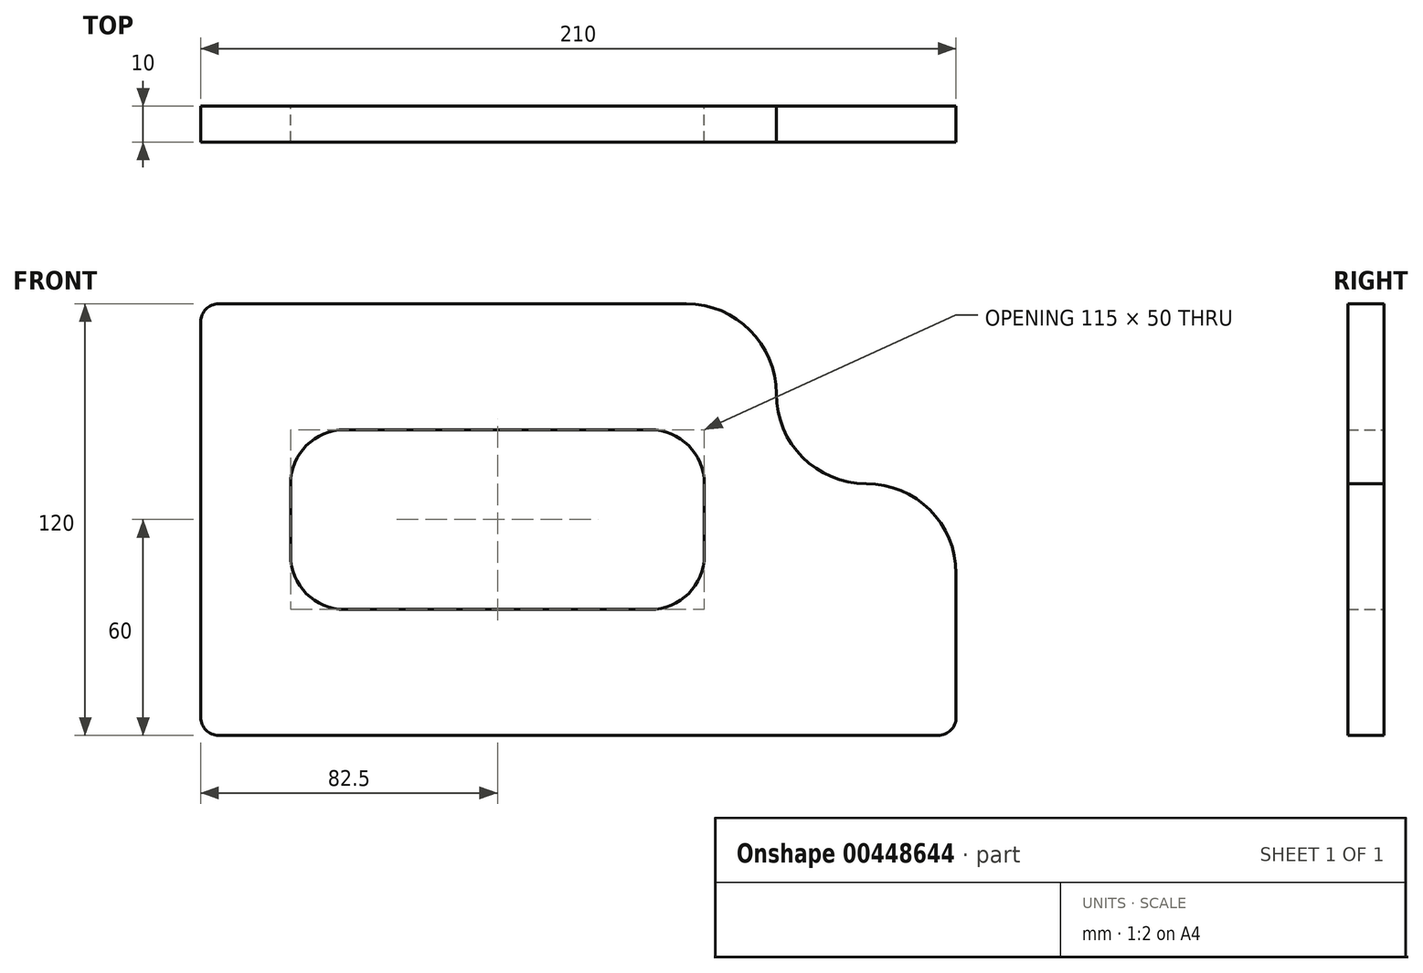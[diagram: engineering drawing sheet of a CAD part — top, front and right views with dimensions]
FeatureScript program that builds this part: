
annotation { "Feature Type Name" : "Feature", "Feature Type Description" : "" }
export const myFeature = defineFeature(function(context is Context, id is Id, definition is map)
    precondition{}
    {
        {
            var Q0;
            Q0=qCreatedBy(makeId("Front.planeOp"),FACE);
            var sketch = newSketch(context, id + "F0", { "sketchPlane" : qUnion([Q0])});
            skLineSegment(sketch, "E0.bottom", {"start": v(-105, 60) * mm, "end": v(55, 60) * mm});
            skLineSegment(sketch, "E0.top", {"start": v(-105, -60) * mm, "end": v(105, -60) * mm});
            skLineSegment(sketch, "E0.left", {"start": v(-105, 60) * mm, "end": v(-105, -60) * mm});
            skLineSegment(sketch, "E0.right", {"start": v(105, 10) * mm, "end": v(105, -60) * mm});
            skPoint(sketch, "E0.middle", {"position": v(0, 0) * mm});
            skLineSegment(sketch, "E1", {"start": v(55, 60) * mm, "end": v(55, 10) * mm});
            skLineSegment(sketch, "E2", {"start": v(55, 10) * mm, "end": v(105, 10) * mm});
            skPoint(sketch, "E3.orphan", {"position": v(105, 60) * mm});
            skLineSegment(sketch, "E4.bottom", {"start": v(-80, 25) * mm, "end": v(35, 25) * mm});
            skLineSegment(sketch, "E4.top", {"start": v(-80, -25) * mm, "end": v(35, -25) * mm});
            skLineSegment(sketch, "E4.left", {"start": v(-80, 25) * mm, "end": v(-80, -25) * mm});
            skLineSegment(sketch, "E4.right", {"start": v(35, 25) * mm, "end": v(35, -25) * mm});
            skSolve(sketch);
        }
        {
            var Q0;
            Q0=makeQuery(id+"F0.imprint","IMPRINT",FACE,{"disambiguationData":[TD([[makeQuery(id+"F0.imprint","IMPRINT",EDGE,{"derivedFrom":sQuery(id+"F0.wireOp",EDGE,"E0.bottom")}),-1.0]])]});
            extrude(context, id + "F1", {"entities" : qUnion([Q0]), "endBound" : BoundingType.SYMMETRIC, "depth" : 10 * mm});
        }
        {
            var Q0;
            Q0=makeQuery(id+"F1.opExtrude","SWEPT_EDGE",EDGE,{"disambiguationData":[OSD([sQuery(id+"F0.wireOp",EDGE,"E1"),sQuery(id+"F0.wireOp",EDGE,"E2")])]});
            var Q1;
            Q1=makeQuery(id+"F1.opExtrude","SWEPT_EDGE",EDGE,{"disambiguationData":[OSD([sQuery(id+"F0.wireOp",EDGE,"E0.right"),sQuery(id+"F0.wireOp",EDGE,"E2")])]});
            var Q2;
            Q2=makeQuery(id+"F1.opExtrude","SWEPT_EDGE",EDGE,{"disambiguationData":[OSD([sQuery(id+"F0.wireOp",EDGE,"E0.bottom"),sQuery(id+"F0.wireOp",EDGE,"E1")])]});
            fillet(context, id + "F2", {"entities" : qUnion([Q0, Q1, Q2]), "radius" : 25 * mm, "tangentPropagation" : true, "allowEdgeOverflow" : false});
        }
        {
            var Q0;
            Q0=makeQuery(id+"F1.opExtrude","SWEPT_EDGE",EDGE,{"disambiguationData":[OSD([sQuery(id+"F0.wireOp",EDGE,"E0.top"),sQuery(id+"F0.wireOp",EDGE,"E0.right")])]});
            var Q1;
            Q1=makeQuery(id+"F1.opExtrude","SWEPT_EDGE",EDGE,{"disambiguationData":[OSD([sQuery(id+"F0.wireOp",EDGE,"E0.top"),sQuery(id+"F0.wireOp",EDGE,"E0.left")])]});
            var Q2;
            Q2=makeQuery(id+"F1.opExtrude","SWEPT_EDGE",EDGE,{"disambiguationData":[OSD([sQuery(id+"F0.wireOp",EDGE,"E0.bottom"),sQuery(id+"F0.wireOp",EDGE,"E0.left")])]});
            fillet(context, id + "F3", {"entities" : qUnion([Q0, Q1, Q2]), "radius" : 5 * mm, "tangentPropagation" : true, "allowEdgeOverflow" : false});
        }
        {
            var Q0;
            Q0=makeQuery(id+"F1.opExtrude","SWEPT_EDGE",EDGE,{"disambiguationData":[OSD([sQuery(id+"F0.wireOp",EDGE,"E4.top"),sQuery(id+"F0.wireOp",EDGE,"E4.left")])]});
            var Q1;
            Q1=makeQuery(id+"F1.opExtrude","SWEPT_EDGE",EDGE,{"disambiguationData":[OSD([sQuery(id+"F0.wireOp",EDGE,"E4.top"),sQuery(id+"F0.wireOp",EDGE,"E4.right")])]});
            var Q2;
            Q2=makeQuery(id+"F1.opExtrude","SWEPT_EDGE",EDGE,{"disambiguationData":[OSD([sQuery(id+"F0.wireOp",EDGE,"E4.bottom"),sQuery(id+"F0.wireOp",EDGE,"E4.right")])]});
            var Q3;
            Q3=makeQuery(id+"F1.opExtrude","SWEPT_EDGE",EDGE,{"disambiguationData":[OSD([sQuery(id+"F0.wireOp",EDGE,"E4.bottom"),sQuery(id+"F0.wireOp",EDGE,"E4.left")])]});
            fillet(context, id + "F4", {"entities" : qUnion([Q0, Q1, Q2, Q3]), "radius" : 15 * mm, "tangentPropagation" : true, "allowEdgeOverflow" : false});
        }
    });
